# Revit family: NTO_MorseTableSection_NOMSDU30
name_source: partatom
category: Furniture
units: mm (PartAtom-declared; Revit-internal decimal feet)

## family parameters
Always vertical = Yes
Cut with Voids When Loaded = No
Room Calculation Point = No
Shared = Yes
Work Plane-Based = No

## types (4) — shared parameters
AssetType = Moveable
BIMObjectName = NTO_Pippin_LoungeChair
Category = Pr_40_50_12_48 : Lounge Chairs
Color = Black legs, RAL 9005. Black underframe, RAL 9005. White MFMDF top with matching edge.
Dot Material = NTO_Finish_Oak
DurationUnit = Year
ExpectedLife = 10
Features = Legs available in 16 RALs + Oak. Underframe available in 16 RALs. Table top available in White or black MFMDF,  or Forbo Desktop Lino (except for Burgundy) with matching edge colour.
Finish = Steel leg and underframe. MFMDF top.
IfcExportAs = IfcFurnitureType
IfcExportType = Chair
Keynote = NOPIP10GLN
NOPIP10GLN
Leg Hardware Material = NTO_FinishBlack_RAL9005
Leg Material = NTO_Finish_Oak
MainColor = Offwhite Upholstery
Manufacturer = NaughtOne
ManufacturerName = NaughtOne
ManufacturerURL = www.naughtone.com
Material = Legs in steel or solid oak. Underframe in steel. Top in MFMDF, or Forbo Lino bonded to MDF. Colour matched edge.
Model = Pippin Lounge Chair
NBSDescription = Chair
NBSReference = 45-35-72/352
Name = Pippin Lounge Chair
ProductInformation = www.naughtone.com/products/pippin
Shape = Rectangular
TableTopMaterial = NTO_Finish_TableTopWhite
URL = www.naughtone.com
Uniclass2015Code = Pr_40_50_12_48
Uniclass2015Title = Lounge Chairs
Uniclass2015Version = Products v1.30
Version = 1
WarrantyDescription = 10 Years
WarrantyDurationUnit = Year
zero-valued in all types: Default Elevation

## per-type parameters (varying)
| type | Description | Dot Visible | LegHeight | ModelReference | MorseBarHeightLegSetD1400D_MSLGD5 | MorseLegSetD1400D_MSLGD3 | Size |
| NOMSDU305B | Morse Bar Heught Table Section Curve 30 deg D - 1400D, with Dot | Yes | 1025 mm  [stored 3.36286 ft] | Morse Bar Heught Table Section Curve 30 deg D - 1400D, with Dot | Yes | No | 1000 x 1480 x 1050 mm |
| NOMSDU305A | Morse Bar Heught Table Section Curve 30 deg D - 1400D | No | 1025 mm  [stored 3.36286 ft] | Morse Bar Heught Table Section Curve 30 deg D - 1400D | Yes | No | 1000 x 1480 x 1050 mm |
| NOMSDU303B | Morse Table Section Curve 30 deg D - 1400D, with Dot | Yes | 705 mm  [stored 2.31299 ft] | Morse Table Section Curve 30 deg D - 1400D, with Dot | No | Yes | 1000 x 1480 x 730 mm |
| NOMSDU303A | Morse Table Section Curve 30 deg D - 1400D | No | 705 mm  [stored 2.31299 ft] | Morse Table Section Curve 30 deg D - 1400D | No | Yes | 1000 x 1480 x 730 mm |

note: column(s) folded — value = type name in every type: ModelNumber

note: [stored X ft] marks values corroborated as IEEE doubles in the binary element streams (Revit-internal decimal feet)

## geometry (parser evidence)
native form markers: Sweep x13
no freeform markers — native parametric forms only
